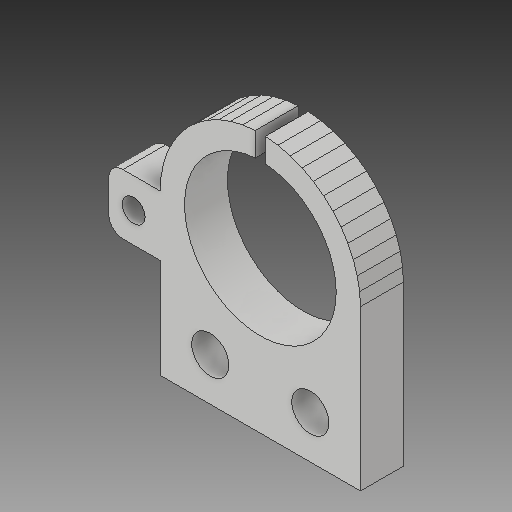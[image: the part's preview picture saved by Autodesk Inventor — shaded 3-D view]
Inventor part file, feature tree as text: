
AUTODESK INVENTOR PART (.ipt)
format: ipt  version: 2017 (Build 210142000, 142)  size: 182,784 bytes
history: native  units: mm
features: other x3, sketch x2
ambient origin geometry x8: Origin, YZ Plane, XZ Plane, XY Plane, X Axis, Y Axis, Z Axis, Center Point
bodies: Solid1 (feature_tree)
feature tree (5):
  other  "Left Bed Holder Upper.ipt"
  other  "Solid1::Left Bed Holder Upper.ipt"
  other  "TaggingFeature1"
  sketch  "Sketch1"  dims[d0=10.0mm]
  sketch  "Sketch3"
